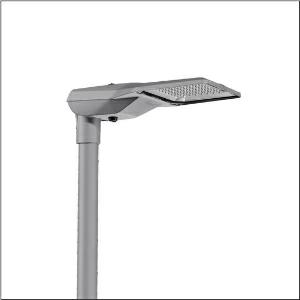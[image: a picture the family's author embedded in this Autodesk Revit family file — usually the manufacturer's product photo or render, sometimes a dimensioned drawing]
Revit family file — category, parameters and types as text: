
# Revit family: streetlight_sl_21_iq_midi___stw1_0a_5xe3e31y08nb_e460
name_source: partatom
category: Lighting Fixtures
units: mm (PartAtom-declared; Revit-internal decimal feet)

## family parameters
Cut with Voids When Loaded = No
Host = Face
Light Source = No
Part Type = Normal
Room Calculation Point = No
Round Connector Dimension = Use Diameter
Shared = No

## types (1)
- --- (1 x LED, 21550 lm, 136.6 W, 3000K)
    Apparent Load = 137 VA
    CIE Flux Codes = 39 75 98 100 100
    Color Rendering = 70
    Color Temperature = 3000K
    Default Elevation = 1800 mm
    Description = Streetlight SL 21 iQ midi, mast luminaire, primary light control with lens, of PMMA, primary optical cover: cover, of toughened safety glass, transparent, light distribution: STW1.0a, light emission: direct distribution, primary light characteristic: asymmetric, installation type: post-top, side-entry, LED, High Power LED, rated luminous flux: 21.550lm, luminous efficacy: 158lm/W, light colour: 730, colour temperature: 3000K, control: presetting dimming logarithmic, Street-Remote, Auto-Match, Temp-Guard, Lumen-Switch, Night-Set, Smart-Wire, Light-Fading, Desk-Remote (wireless, voltage-free reading and setting of iQ features in the workshop via application-optimized NFC function/RFID function), optimised constant luminous flux control (CLO 2.0), mains connection: 230..240V, AC, 50/60Hz, start of lifetime: 137W, end of service life: 144W, reduction: 61W, luminaire housing, of diecast aluminium, powder-coated, Siteco® metallic grey (DB 702S), corrosivity category C5 mid according to DIN EN ISO 12944, please order mast flange separately, inclination adjustable: 0°, 5°, 10°, 15°, sealing non-destructively replaceable, multi-level sealing system, length: 644mm, width: 335mm, height: 110mm, mast flange for spigot size: 42mm (side-entry): 5XC10008XM4, 60/48mm (side-entry/post-top): 5XC10108XM2, 76/60mm (side-entry/post-top): 5XC10108XM1, Smart Interface below and above, protection rating (complete): IP66, insulation class (complete): insulation class II (safety insulation), certification: CE, ENEC, ENEC+, VDE, impact resistance: IK09, permissible operating ambient temperature for outdoor applications: -40..+50°C, standard-compliant lighting for roads and squares, packaging unit: 1 piece

Light Distribution: STW1.0a
    Height = 111 mm
    Lamp = 1 x LED
    Lamp Light Flux = 21550 lm
    Lamp Power = 136.6 W
    Lamp count = 1
    Length = 644 mm
    Luminous efficacy = 158 lm/W
    Manufacturer = Siteco
    ModVariant = No
    Model = 5XE3E31Y08NB
    Number of Poles = 1
    OnlyDefault = Yes
    Power Factor = 1
    Product Name = Streetlight SL 21 iQ midi | STW1.0a
    Product group = mast luminaire | pylon top
    ProductGroupID = 6100
    Protection Class = Protection class II
    Protection Degree = IP 66
    RLX_Detail_Level = 1
    RLX_Emergency_Light_Flux = 0 lm
    RLX_Emergency_Type = 0
    RLX_Emergency_Type_DB = No
    RlxData = <blob elided: 90785 chars, md5=ccfc4d67>
    Socket = socket
    Standby Power = 0 W
    System Light Flux = 21550 lm
    System Power = 137 W
    Type Comments = factory setting: luminous flux: 100 % | dim-lin: 254 | 733 mA
    Type Image = l_1004304.jpg
    URL = http://relux.com
    VarID = @adj_043693
    Voltage = 0 V
    Weight = 0.00 kg
    Width = 336 mm

## geometry (parser evidence)
native form markers: Blend x4, Sweep x12
no freeform markers — native parametric forms only
